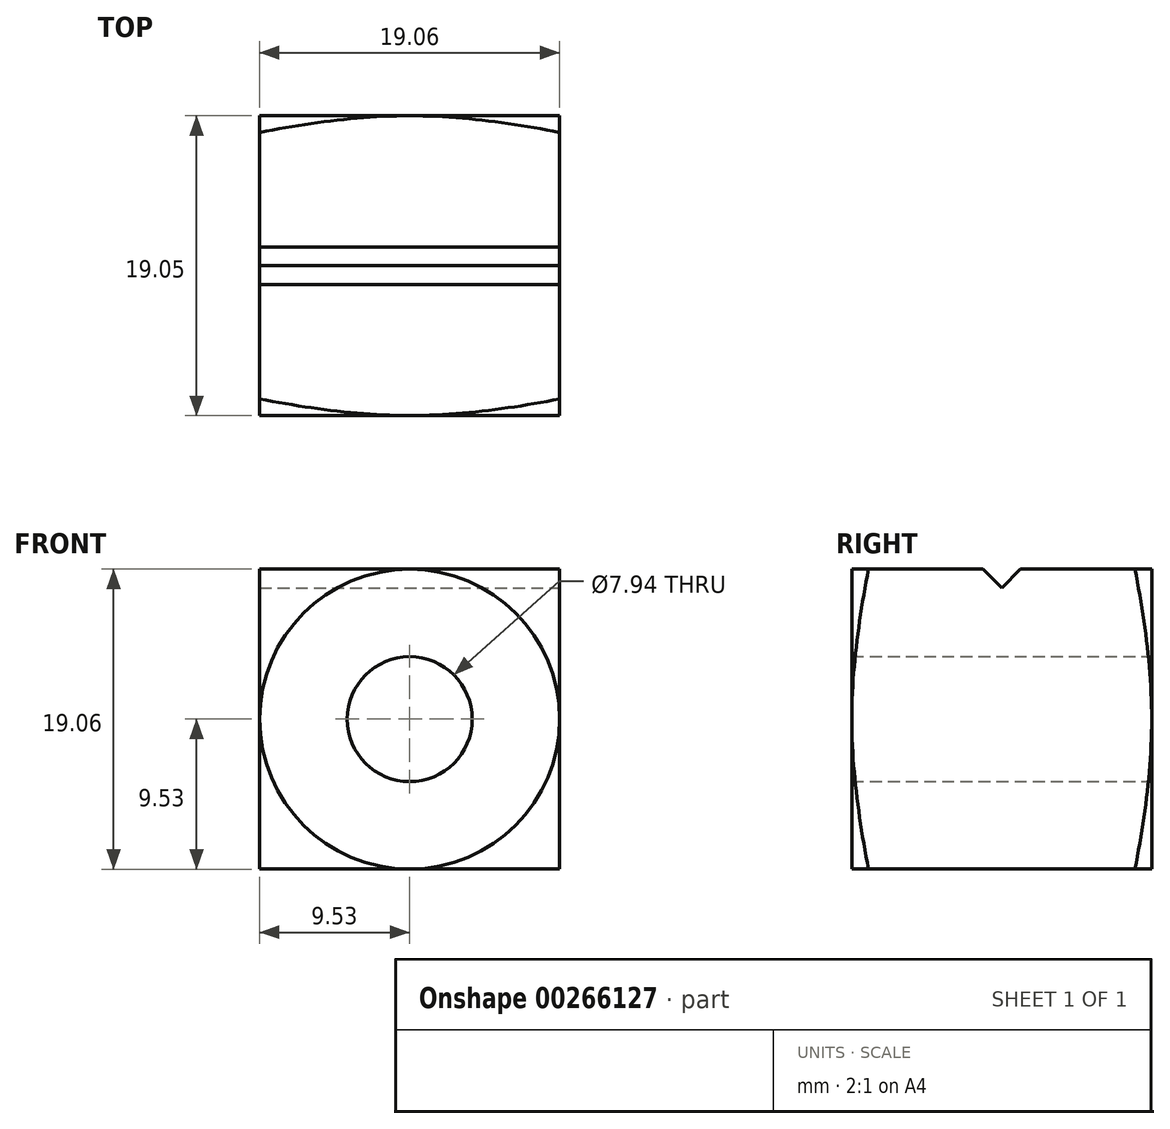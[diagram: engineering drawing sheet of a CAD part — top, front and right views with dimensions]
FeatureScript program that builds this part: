
annotation { "Feature Type Name" : "Feature", "Feature Type Description" : "" }
export const myFeature = defineFeature(function(context is Context, id is Id, definition is map)
    precondition{}
    {
        {
            var Q0;
            Q0=qCreatedBy(makeId("Front.planeOp"),FACE);
            var sketch = newSketch(context, id + "F0", { "sketchPlane" : qUnion([Q0])});
            skCircle(sketch, "E0", {"center": v(0, 0) * mm, "radius": 9.52 * mm});
            skLineSegment(sketch, "E1.bottom", {"start": v(9.53, 9.53) * mm, "end": v(-9.53, 9.53) * mm});
            skLineSegment(sketch, "E1.top", {"start": v(9.53, -9.53) * mm, "end": v(-9.53, -9.53) * mm});
            skLineSegment(sketch, "E1.left", {"start": v(9.53, 9.53) * mm, "end": v(9.53, -9.53) * mm});
            skLineSegment(sketch, "E1.right", {"start": v(-9.53, 9.53) * mm, "end": v(-9.53, -9.53) * mm});
            skCircle(sketch, "E2", {"center": v(0, 0) * mm, "radius": 3.97 * mm});
            skSolve(sketch);
        }
        {
            var Q0;
            Q0 = qSketchRegion(id + "F0", true);
            extrude(context, id + "F1", {"entities" : qUnion([Q0]), "depth" : 19.05 * mm});
        }
        {
            var Q0;
            Q0=makeQuery(id+"F1.opExtrude","SWEPT_FACE",FACE,{"disambiguationData":[OSD([sQuery(id+"F0.wireOp",EDGE,"E1.left")])]});
            var sketch = newSketch(context, id + "F2", { "sketchPlane" : qUnion([Q0])});
            skLineSegment(sketch, "E3", {"start": v(-9.53, 9.53) * mm, "end": v(-9.53, -9.53) * mm, "construction": true});
            skLineSegment(sketch, "E4", {"start": v(-9.53, 8.33) * mm, "end": v(-4.66, 13.2) * mm});
            skLineSegment(sketch, "E5", {"start": v(-4.66, 13.2) * mm, "end": v(-14.39, 13.2) * mm});
            skLineSegment(sketch, "E6", {"start": v(-14.39, 13.2) * mm, "end": v(-9.53, 8.33) * mm});
            skSolve(sketch);
        }
        {
            var Q0;
            Q0 = qSketchRegion(id + "F2", true);
            extrude(context, id + "F3", {"entities" : qUnion([Q0]), "operationType" : NewBodyOperationType.REMOVE, "oppositeDirection" : true, "depth" : 127 * mm});
        }
        {
            var Q0;
            Q0=qCreatedBy(makeId("Right.planeOp"),FACE);
            var sketch = newSketch(context, id + "F4", { "sketchPlane" : qUnion([Q0])});
            skLineSegment(sketch, "E7.0.0", {"start": v(-9.53, 8.33) * mm, "end": v(-10.72, 9.53) * mm});
            skLineSegment(sketch, "E7.0.1", {"start": v(-10.72, 9.53) * mm, "end": v(-19.05, 9.53) * mm});
            skLineSegment(sketch, "E7.0.2", {"start": v(-19.05, 9.53) * mm, "end": v(-19.05, -9.53) * mm});
            skLineSegment(sketch, "E7.0.3", {"start": v(-19.05, -9.53) * mm, "end": v(0, -9.53) * mm});
            skLineSegment(sketch, "E7.0.4", {"start": v(0, -9.53) * mm, "end": v(0, 9.53) * mm});
            skLineSegment(sketch, "E7.0.5", {"start": v(0, 9.53) * mm, "end": v(-8.33, 9.53) * mm});
            skLineSegment(sketch, "E7.0.6", {"start": v(-8.33, 9.53) * mm, "end": v(-9.53, 8.33) * mm});
            skLineSegment(sketch, "E8", {"start": v(-19.05, 9.53) * mm, "end": v(-19.05, 15.17) * mm});
            skLineSegment(sketch, "E9", {"start": v(-19.05, 15.17) * mm, "end": v(-17.54, 15.17) * mm});
            skLineSegment(sketch, "E10", {"start": v(-17.54, 15.17) * mm, "end": v(-19.05, 9.53) * mm});
            skSolve(sketch);
        }
        {
            var Q0;
            Q0=makeQuery(id+"F4.imprint","IMPRINT",FACE,{"disambiguationData":[TD([[makeQuery(id+"F4.imprint","IMPRINT",EDGE,{"derivedFrom":sQuery(id+"F4.wireOp",EDGE,"E8")}),-1.0]])]});
            var Q1;
            Q1=makeQuery(id+"F1.opExtrude","CAP_EDGE",EDGE,{"disambiguationData":[OSD([sQuery(id+"F0.wireOp",EDGE,"E2")])],"isStart":false});
            revolve(context, id + "F5", {"operationType" : NewBodyOperationType.REMOVE, "entities" : qUnion([Q0]), "axis" : qUnion([Q1]), "revolveType" : RevolveType.FULL, "oppositeDirection" : true});
        }
        {
            var Q0;
            Q0=qCreatedBy(makeId("Right.planeOp"),FACE);
            var sketch = newSketch(context, id + "F6", { "sketchPlane" : qUnion([Q0])});
            skFitSpline(sketch, "E11.0.0", {"points": [v(-19.05, 0) * mm, v(-19.05, -0.8) * mm, v(-19, -2.39) * mm, v(-18.7, -5.57) * mm, v(-18.3, -7.95) * mm, v(-18, -9.53) * mm]});
            skLineSegment(sketch, "E11.0.1", {"start": v(-18, -9.53) * mm, "end": v(0, -9.53) * mm});
            skLineSegment(sketch, "E11.0.2", {"start": v(0, -9.53) * mm, "end": v(0, 9.53) * mm});
            skLineSegment(sketch, "E11.0.3", {"start": v(0, 9.53) * mm, "end": v(-8.33, 9.53) * mm});
            skLineSegment(sketch, "E11.0.4", {"start": v(-8.33, 9.53) * mm, "end": v(-9.53, 8.33) * mm});
            skLineSegment(sketch, "E11.0.5", {"start": v(-9.53, 8.33) * mm, "end": v(-10.72, 9.53) * mm});
            skLineSegment(sketch, "E11.0.6", {"start": v(-10.72, 9.53) * mm, "end": v(-18, 9.53) * mm});
            skFitSpline(sketch, "E11.0.7", {"points": [v(-18, 9.53) * mm, v(-18.14, 8.74) * mm, v(-18.42, 7.16) * mm, v(-18.77, 4.78) * mm, v(-19, 2.39) * mm, v(-19.05, 0.8) * mm, v(-19.05, 0) * mm]});
            skLineSegment(sketch, "E12", {"start": v(0, 9.53) * mm, "end": v(0, 14.69) * mm});
            skLineSegment(sketch, "E13", {"start": v(0, 14.69) * mm, "end": v(-1.38, 14.69) * mm});
            skLineSegment(sketch, "E14", {"start": v(-1.38, 14.69) * mm, "end": v(0, 9.53) * mm});
            skSolve(sketch);
        }
        {
            var Q0;
            Q0=makeQuery(id+"F6.imprint","IMPRINT",FACE,{"disambiguationData":[TD([[makeQuery(id+"F6.imprint","IMPRINT",EDGE,{"derivedFrom":sQuery(id+"F6.wireOp",EDGE,"E12")}),1.0]])]});
            var Q1;
            Q1=makeQuery(id+"F1.opExtrude","CAP_EDGE",EDGE,{"disambiguationData":[OSD([sQuery(id+"F0.wireOp",EDGE,"E2")])],"isStart":true});
            revolve(context, id + "F7", {"operationType" : NewBodyOperationType.REMOVE, "entities" : qUnion([Q0]), "axis" : qUnion([Q1]), "revolveType" : RevolveType.FULL, "oppositeDirection" : true});
        }
    });
